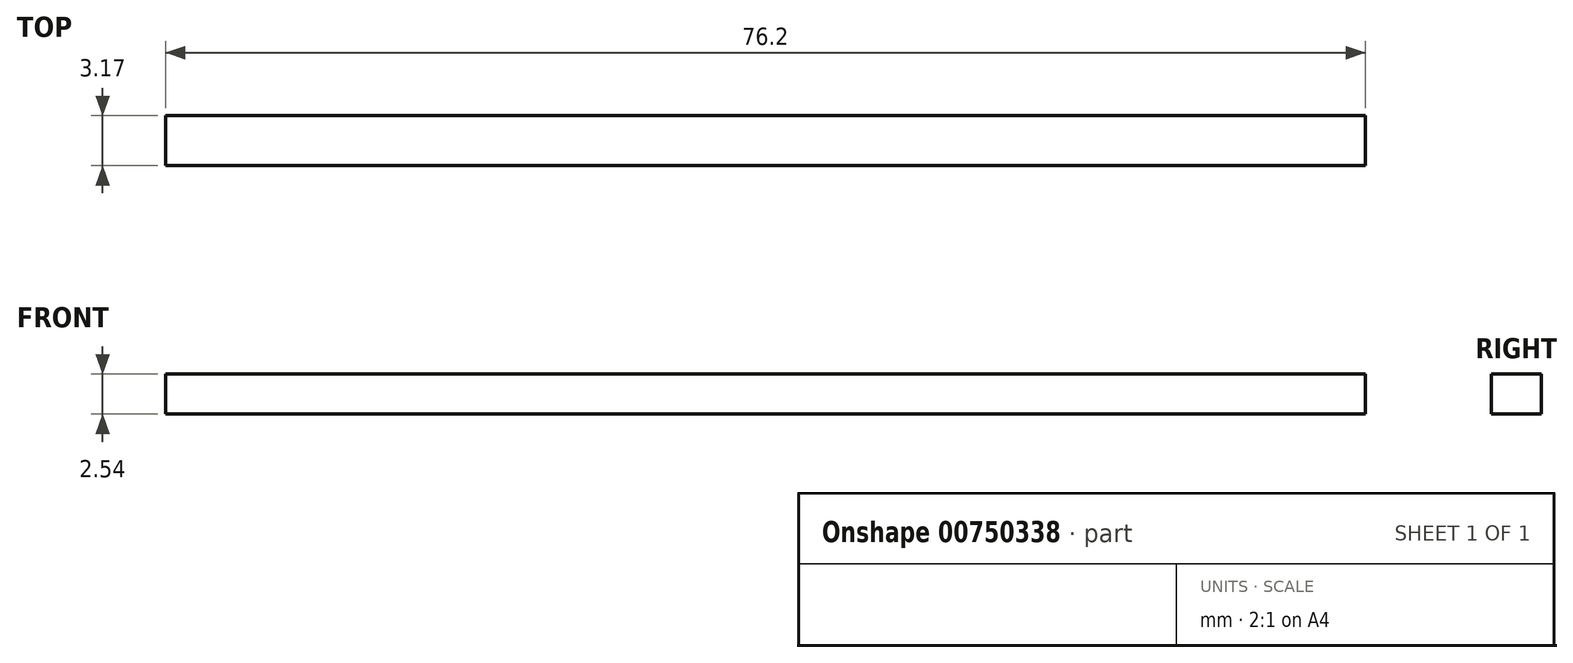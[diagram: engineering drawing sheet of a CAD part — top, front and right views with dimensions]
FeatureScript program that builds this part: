
annotation { "Feature Type Name" : "Feature", "Feature Type Description" : "" }
export const myFeature = defineFeature(function(context is Context, id is Id, definition is map)
    precondition{}
    {
        {
            var Q0;
            Q0=qCreatedBy(makeId("Front.planeOp"),FACE);
            var sketch = newSketch(context, id + "F0", { "sketchPlane" : qUnion([Q0])});
            skLineSegment(sketch, "E0.bottom", {"start": v(-23.76, -2.65) * mm, "end": v(52.44, -2.65) * mm});
            skLineSegment(sketch, "E0.top", {"start": v(-23.76, -5.19) * mm, "end": v(52.44, -5.19) * mm});
            skLineSegment(sketch, "E0.left", {"start": v(-23.76, -2.65) * mm, "end": v(-23.76, -5.19) * mm});
            skLineSegment(sketch, "E0.right", {"start": v(52.44, -2.65) * mm, "end": v(52.44, -5.19) * mm});
            skSolve(sketch);
        }
        {
            var Q0;
            Q0=makeQuery(id+"F0.imprint","IMPRINT",FACE,{"disambiguationData":[TD([[makeQuery(id+"F0.imprint","IMPRINT",EDGE,{"derivedFrom":sQuery(id+"F0.wireOp",EDGE,"E0.bottom")}),-1.0]])]});
            extrude(context, id + "F1", {"entities" : qUnion([Q0]), "depth" : 3.17 * mm, "offsetDistance" : 25.4 * mm});
        }
    });
